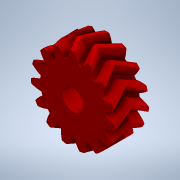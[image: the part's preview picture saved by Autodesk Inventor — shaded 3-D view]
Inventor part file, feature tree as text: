
AUTODESK INVENTOR PART (.ipt)
format: ipt  version: 2020 (Build 240168000, 168)  size: 566,272 bytes
history: native  units: mm (DEFAULTED — no unit token found)
features: extrude x3, plane x3, other x3, sketch x3, mirror x1
ambient origin geometry x8: Origin, YZ Plane, XZ Plane, XY Plane, X Axis, Y Axis, Z Axis, Center Point
bodies: Solid1 (feature_tree)
feature tree (13):
  extrude  "Extrusion1"  Depth=5.0mm TaperAngle=0.0deg
  plane  "Work Plane2"
  plane  "Work Plane8"
  plane  "Work Plane9"
  other  "Spur Gear"
  mirror  "Mirror1"
  sketch  "Sketch3"  dims[d16=22.2mm d17=0.0mm d34=2.094395mm d39=0.0mm d41=0.0mm d43=22.2mm d46=22.2mm d47=0.0mm d48=0.0mm d49=6.0mm d50=10.0mm d51=0.0mm d52=3.0mm d53=3.0mm d54=3.0mm d55=3.0mm d57=14.0mm d58=6.0mm d59=0.0mm]
  extrude  "Extrusion2"  Depth=10.0mm TaperAngle=0.0deg
  extrude  "Extrusion3"  Depth=6.0mm TaperAngle=0.0deg
  sketch  "Sketch1"  dims[d0=24.663139mm d1=5.0mm d2=0.0mm]
  sketch  "Sketch2"  dims[d3=22.2mm d4=10.0mm d5=0.0mm]
  other  "Srf1"
  other  "Pitch Diameter"
